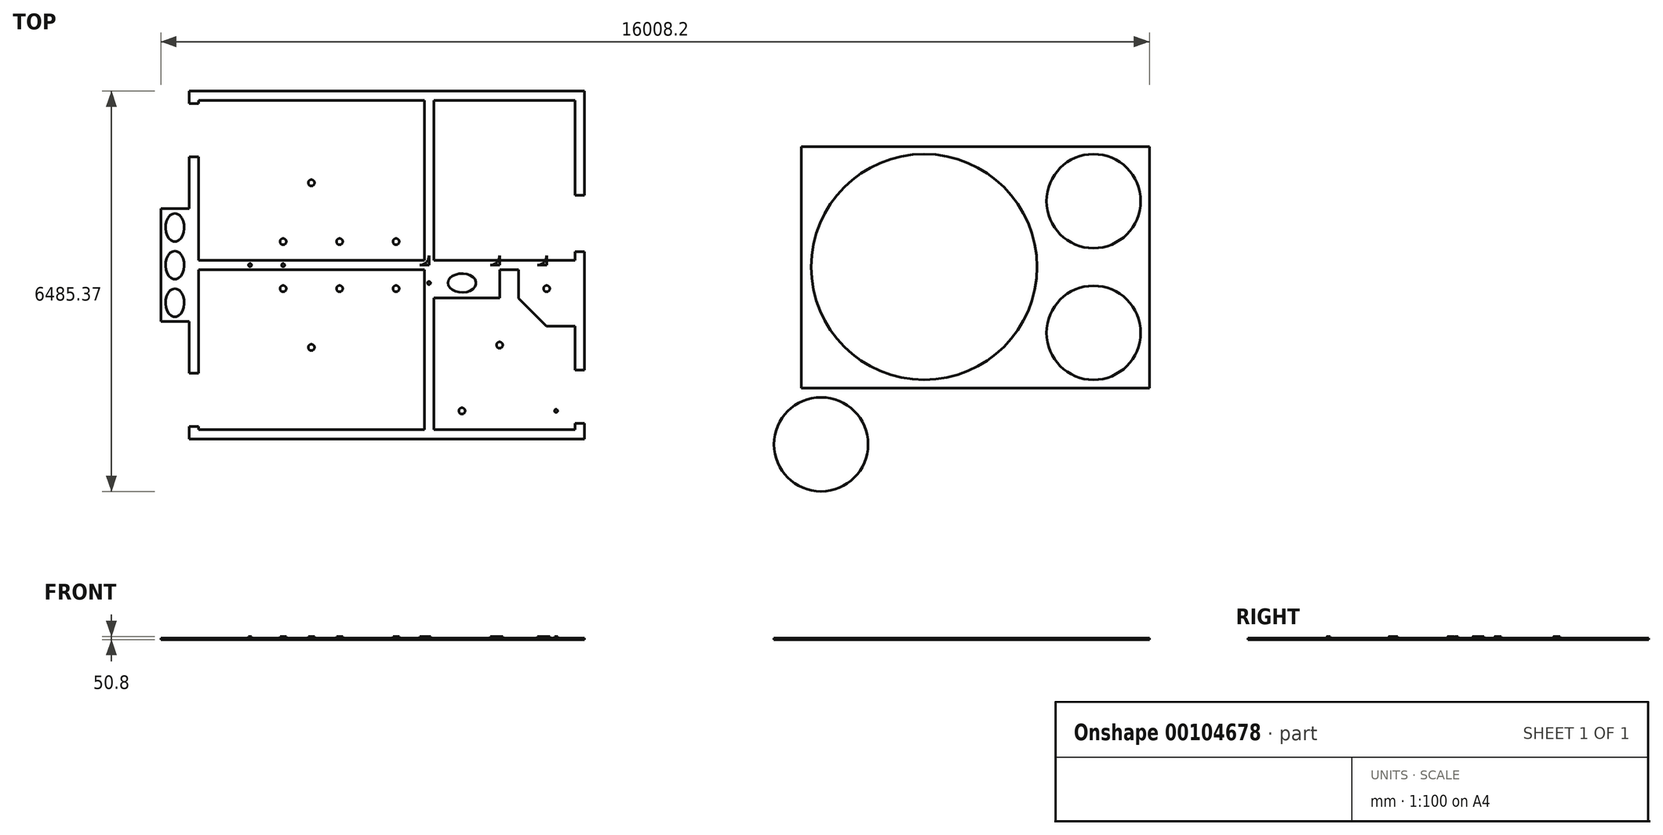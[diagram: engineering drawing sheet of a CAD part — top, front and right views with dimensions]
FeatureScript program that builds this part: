
annotation { "Feature Type Name" : "Feature", "Feature Type Description" : "" }
export const myFeature = defineFeature(function(context is Context, id is Id, definition is map)
    precondition{}
    {
        {
            var Q0;
            Q0=qCreatedBy(makeId("Top.planeOp"),FACE);
            var sketch = newSketch(context, id + "F0", { "sketchPlane" : qUnion([Q0])});
            skLineSegment(sketch, "E0.bottom", {"start": v(0, -6096) * mm, "end": v(7315.2, -6096) * mm, "construction": true});
            skLineSegment(sketch, "E0.left", {"start": v(0, -6096) * mm, "end": v(0, 0) * mm, "construction": true});
            skLineSegment(sketch, "E0.right", {"start": v(7315.2, -6096) * mm, "end": v(7315.2, 0) * mm, "construction": true});
            skLineSegment(sketch, "E1", {"start": v(-8239.1, 0) * mm, "end": v(16647.6, 0) * mm, "construction": true});
            skLineSegment(sketch, "E2", {"start": v(3581.4, 0) * mm, "end": v(3581.4, -228.6) * mm});
            skLineSegment(sketch, "E3", {"start": v(3581.4, -228.6) * mm, "end": v(3733.8, -228.6) * mm});
            skLineSegment(sketch, "E4", {"start": v(3733.8, -228.6) * mm, "end": v(3733.8, 0) * mm});
            skSolve(sketch);
        }
        {
            var Q0;
            Q0=qCreatedBy(makeId("Top.planeOp"),FACE);
            var sketch = newSketch(context, id + "F1", { "sketchPlane" : qUnion([Q0])});
            skLineSegment(sketch, "E5", {"start": v(152.4, -2743.2) * mm, "end": v(3810, -2743.2) * mm});
            skLineSegment(sketch, "E6.MirrorCS", {"start": v(152.4, -2895.6) * mm, "end": v(3810, -2895.6) * mm});
            skLineSegment(sketch, "E7", {"start": v(6400.8, -5638.8) * mm, "end": v(0, -5638.8) * mm});
            skLineSegment(sketch, "E8", {"start": v(0, -4572) * mm, "end": v(0, -1066.8) * mm});
            skLineSegment(sketch, "E9", {"start": v(0, 0) * mm, "end": v(3962.4, 0) * mm});
            skLineSegment(sketch, "E10", {"start": v(3962.4, -152.4) * mm, "end": v(3962.4, -2743.2) * mm});
            skCircle(sketch, "E11", {"center": v(11904.2, -2849.46) * mm, "radius": 1828.8 * mm});
            skCircle(sketch, "E12", {"center": v(14647.4, -3916.26) * mm, "radius": 762 * mm});
            skLineSegment(sketch, "E13", {"start": v(14647.4, -3916.26) * mm, "end": v(14647.4, -1782.66) * mm});
            skCircle(sketch, "E14", {"center": v(14647.4, -1782.66) * mm, "radius": 762 * mm});
            skLineSegment(sketch, "E15", {"start": v(14647.4, -2849.46) * mm, "end": v(11904.2, -2849.46) * mm});
            skLineSegment(sketch, "E16", {"start": v(3962.4, 0) * mm, "end": v(6400.8, 0) * mm});
            skLineSegment(sketch, "E17", {"start": v(6400.8, 0) * mm, "end": v(6400.8, -1687.1) * mm});
            skLineSegment(sketch, "E18", {"start": v(152.4, -2743.2) * mm, "end": v(152.4, -1066.8) * mm});
            skLineSegment(sketch, "E19", {"start": v(3810, -2743.2) * mm, "end": v(3810, -152.4) * mm});
            skLineSegment(sketch, "E20", {"start": v(3810, -152.4) * mm, "end": v(152.4, -152.4) * mm});
            skLineSegment(sketch, "E21", {"start": v(152.4, -1066.8) * mm, "end": v(0, -1066.8) * mm});
            skLineSegment(sketch, "E22.trimOffspring", {"start": v(0, -203.2) * mm, "end": v(0, 0) * mm});
            skLineSegment(sketch, "E23", {"start": v(0, -5638.8) * mm, "end": v(0, -5435.6) * mm});
            skLineSegment(sketch, "E24", {"start": v(3810, -5486.4) * mm, "end": v(3810, -2895.6) * mm});
            skLineSegment(sketch, "E25", {"start": v(2895.6, -2743.2) * mm, "end": v(2895.6, -1219.2) * mm});
            skLineSegment(sketch, "E26", {"start": v(0, -4572) * mm, "end": v(152.4, -4572) * mm});
            skLineSegment(sketch, "E27", {"start": v(152.4, -4572) * mm, "end": v(152.4, -2895.6) * mm});
            skLineSegment(sketch, "E28", {"start": v(1981.2, -2743.2) * mm, "end": v(1981.2, -1219.2) * mm});
            skLineSegment(sketch, "E29", {"start": v(0, -203.2) * mm, "end": v(152.4, -203.2) * mm});
            skLineSegment(sketch, "E30", {"start": v(152.4, -203.2) * mm, "end": v(152.4, -152.4) * mm});
            skLineSegment(sketch, "E31", {"start": v(0, -5435.6) * mm, "end": v(152.4, -5435.6) * mm});
            skLineSegment(sketch, "E32", {"start": v(152.4, -5435.6) * mm, "end": v(152.4, -5486.4) * mm});
            skLineSegment(sketch, "E33.trimOffspring", {"start": v(152.4, -5486.4) * mm, "end": v(3810, -5486.4) * mm});
            skLineSegment(sketch, "E34", {"start": v(1066.8, -2743.2) * mm, "end": v(1066.8, -1219.2) * mm});
            skLineSegment(sketch, "E35", {"start": v(1066.8, -1219.2) * mm, "end": v(1143, -1219.2) * mm});
            skLineSegment(sketch, "E36", {"start": v(1905, -1219.2) * mm, "end": v(2057.4, -1219.2) * mm});
            skLineSegment(sketch, "E37", {"start": v(2819.4, -1219.2) * mm, "end": v(2971.8, -1219.2) * mm});
            skLineSegment(sketch, "E38", {"start": v(1143, -1219.2) * mm, "end": v(1732.48, -1702.06) * mm});
            skLineSegment(sketch, "E39", {"start": v(3810, -1219.2) * mm, "end": v(3733.8, -1219.2) * mm});
            skLineSegment(sketch, "E40", {"start": v(2057.4, -1219.2) * mm, "end": v(2646.88, -1702.06) * mm});
            skLineSegment(sketch, "E41", {"start": v(2971.8, -1219.2) * mm, "end": v(3561.28, -1702.06) * mm});
            skLineSegment(sketch, "E42", {"start": v(76.2, -203.2) * mm, "end": v(589.55, -897.66) * mm});
            skLineSegment(sketch, "E43", {"start": v(6400.8, -2819.4) * mm, "end": v(0, -2819.4) * mm, "construction": true});
            skLineSegment(sketch, "E44.MirrorCS", {"start": v(76.2, -5435.6) * mm, "end": v(589.55, -4741.14) * mm});
            skLineSegment(sketch, "E45.MirrorCS", {"start": v(1066.8, -4419.6) * mm, "end": v(1143, -4419.6) * mm});
            skLineSegment(sketch, "E46.MirrorCS", {"start": v(2819.4, -4419.6) * mm, "end": v(2971.8, -4419.6) * mm});
            skLineSegment(sketch, "E47.MirrorCS", {"start": v(1905, -4419.6) * mm, "end": v(2057.4, -4419.6) * mm});
            skLineSegment(sketch, "E48.MirrorCS", {"start": v(2971.8, -4419.6) * mm, "end": v(3561.28, -3936.74) * mm});
            skLineSegment(sketch, "E49.MirrorCS", {"start": v(1981.2, -2895.6) * mm, "end": v(1981.2, -4419.6) * mm});
            skLineSegment(sketch, "E50.MirrorCS", {"start": v(1066.8, -2895.6) * mm, "end": v(1066.8, -4419.6) * mm});
            skLineSegment(sketch, "E51.MirrorCS", {"start": v(2057.4, -4419.6) * mm, "end": v(2646.88, -3936.74) * mm});
            skLineSegment(sketch, "E52.MirrorCS", {"start": v(2895.6, -2895.6) * mm, "end": v(2895.6, -4419.6) * mm});
            skLineSegment(sketch, "E53.MirrorCS", {"start": v(3810, -4419.6) * mm, "end": v(3733.8, -4419.6) * mm});
            skLineSegment(sketch, "E54.MirrorCS", {"start": v(1143, -4419.6) * mm, "end": v(1732.48, -3936.74) * mm});
            skLineSegment(sketch, "E55", {"start": v(0, -1905) * mm, "end": v(-457.2, -1905) * mm});
            skLineSegment(sketch, "E56", {"start": v(-457.2, -1905) * mm, "end": v(-457.2, -3733.8) * mm});
            skLineSegment(sketch, "E57", {"start": v(-457.2, -3733.8) * mm, "end": v(0, -3733.8) * mm});
            skEllipse(sketch, "E58", {"center": v(-228.6, -2209.8) * mm, "majorRadius": 228.6 * mm, "minorRadius": 152.4 * mm, "majorAxis": v(0, 1)});
            skEllipse(sketch, "E59", {"center": v(-228.6, -2819.4) * mm, "majorRadius": 228.6 * mm, "minorRadius": 152.4 * mm, "majorAxis": v(0, 1)});
            skEllipse(sketch, "E60", {"center": v(-228.6, -3429) * mm, "majorRadius": 228.6 * mm, "minorRadius": 152.4 * mm, "majorAxis": v(0, 1)});
            skLineSegment(sketch, "E61", {"start": v(3962.4, -2895.6) * mm, "end": v(6248.4, -2895.6) * mm});
            skLineSegment(sketch, "E62", {"start": v(6248.4, -2895.6) * mm, "end": v(6248.4, -4521.2) * mm});
            skLineSegment(sketch, "E63.trimOffspring", {"start": v(3962.4, -2895.6) * mm, "end": v(3962.4, -5486.4) * mm});
            skLineSegment(sketch, "E64.trimOffspring", {"start": v(3962.4, -5486.4) * mm, "end": v(6248.4, -5486.4) * mm});
            skLineSegment(sketch, "E65.bottom", {"start": v(15551.04, -4814.37) * mm, "end": v(9912.24, -4814.37) * mm});
            skLineSegment(sketch, "E65.top", {"start": v(15551.04, -902.77) * mm, "end": v(9912.24, -902.77) * mm});
            skLineSegment(sketch, "E65.left", {"start": v(15551.04, -4814.37) * mm, "end": v(15551.04, -902.77) * mm});
            skLineSegment(sketch, "E65.right", {"start": v(9912.24, -4814.37) * mm, "end": v(9912.24, -902.77) * mm});
            skEllipse(sketch, "E66", {"center": v(4419.6, -3109.6) * mm, "majorRadius": 228.6 * mm, "minorRadius": 152.4 * mm, "majorAxis": v(-1, 0)});
            skLineSegment(sketch, "E67", {"start": v(3962.4, -3352.8) * mm, "end": v(5029.2, -3352.8) * mm});
            skLineSegment(sketch, "E68", {"start": v(6248.4, -3810) * mm, "end": v(5784.85, -3810) * mm});
            skCircle(sketch, "E69", {"center": v(10234.54, -5723.37) * mm, "radius": 762 * mm});
            skLineSegment(sketch, "E70", {"start": v(5334, -3359.15) * mm, "end": v(5784.85, -3810) * mm});
            skLineSegment(sketch, "E71.trimOffspring", {"start": v(5334, -3359.15) * mm, "end": v(5334, -2895.6) * mm});
            skLineSegment(sketch, "E72", {"start": v(3962.4, -152.4) * mm, "end": v(6248.4, -152.4) * mm});
            skLineSegment(sketch, "E73", {"start": v(6248.4, -152.4) * mm, "end": v(6248.4, -1687.1) * mm});
            skLineSegment(sketch, "E74", {"start": v(6248.4, -2743.2) * mm, "end": v(3962.4, -2743.2) * mm});
            skLineSegment(sketch, "E75", {"start": v(6248.4, -2601.5) * mm, "end": v(6400.8, -2601.5) * mm});
            skLineSegment(sketch, "E76", {"start": v(6248.4, -1687.1) * mm, "end": v(6400.8, -1687.1) * mm});
            skLineSegment(sketch, "E77.trimOffspring", {"start": v(6248.4, -2601.5) * mm, "end": v(6248.4, -2743.2) * mm});
            skLineSegment(sketch, "E78.trimOffspring", {"start": v(6400.8, -2601.5) * mm, "end": v(6400.8, -4521.2) * mm});
            skLineSegment(sketch, "E79", {"start": v(5029.2, -3352.8) * mm, "end": v(5029.2, -2895.6) * mm});
            skCircle(sketch, "E80", {"center": v(4419.6, -5181.6) * mm, "radius": 50.8 * mm});
            skLineSegment(sketch, "E81", {"start": v(6248.4, -5384.8) * mm, "end": v(6400.8, -5384.8) * mm});
            skLineSegment(sketch, "E82", {"start": v(6248.4, -4521.2) * mm, "end": v(6400.8, -4521.2) * mm});
            skLineSegment(sketch, "E83.trimOffspring", {"start": v(6400.8, -5384.8) * mm, "end": v(6400.8, -5638.8) * mm});
            skLineSegment(sketch, "E84.trimOffspring", {"start": v(6248.4, -5384.8) * mm, "end": v(6248.4, -5486.4) * mm});
            skLineSegment(sketch, "E85", {"start": v(6324.6, -5384.8) * mm, "end": v(5921.52, -4621.04) * mm});
            skLineSegment(sketch, "E86", {"start": v(6324.6, -2601.5) * mm, "end": v(5876.55, -1804.4) * mm});
            skPoint(sketch, "E87", {"position": v(5105.4, -1447.8) * mm});
            skLineSegment(sketch, "E88", {"start": v(5105.4, -1447.8) * mm, "end": v(4404.46, -2148.74) * mm});
            skLineSegment(sketch, "E89", {"start": v(5105.4, -1447.8) * mm, "end": v(5105.4, -2236.51) * mm, "construction": true});
            skSolve(sketch);
        }
        {
            var Q0;
            Q0=qCreatedBy(makeId("Top.planeOp"),FACE);
            var sketch = newSketch(context, id + "F2", { "sketchPlane" : qUnion([Q0])});
            skLineSegment(sketch, "E90", {"start": v(5791.2, -2667) * mm, "end": v(5791.2, -3251.2) * mm});
            skCircle(sketch, "E91", {"center": v(1524, -2438.4) * mm, "radius": 50.8 * mm});
            skCircle(sketch, "E92", {"center": v(1524, -3200.4) * mm, "radius": 50.8 * mm});
            skCircle(sketch, "E93", {"center": v(2438.4, -3200.4) * mm, "radius": 50.8 * mm});
            skCircle(sketch, "E94", {"center": v(2438.4, -2438.4) * mm, "radius": 50.8 * mm});
            skCircle(sketch, "E95", {"center": v(3352.8, -2438.4) * mm, "radius": 50.8 * mm});
            skCircle(sketch, "E96", {"center": v(3352.8, -3200.4) * mm, "radius": 50.8 * mm});
            skCircle(sketch, "E97", {"center": v(5791.2, -3200.4) * mm, "radius": 50.8 * mm});
            skCircle(sketch, "E98", {"center": v(3886.2, -3109.6) * mm, "radius": 25.4 * mm});
            skCircle(sketch, "E99", {"center": v(988.97, -2819.4) * mm, "radius": 25.4 * mm});
            skCircle(sketch, "E100", {"center": v(1981.2, -4152.9) * mm, "radius": 50.8 * mm});
            skCircle(sketch, "E101", {"center": v(1981.2, -1485.9) * mm, "radius": 50.8 * mm});
            skCircle(sketch, "E102", {"center": v(5029.2, -4114.8) * mm, "radius": 50.8 * mm});
            skLineSegment(sketch, "E103", {"start": v(1981.2, -1485.9) * mm, "end": v(1981.2, -2794.35) * mm});
            skLineSegment(sketch, "E104", {"start": v(1981.2, -4152.9) * mm, "end": v(1981.2, -2844.46) * mm});
            skLineSegment(sketch, "E105", {"start": v(5029.2, -2667) * mm, "end": v(5029.2, -4165.6) * mm});
            skLineSegment(sketch, "E106", {"start": v(0, -2819.4) * mm, "end": v(1834.75, -2819.4) * mm});
            skLineSegment(sketch, "E107", {"start": v(1524, -2489.2) * mm, "end": v(1524, -2813.12) * mm});
            skLineSegment(sketch, "E108", {"start": v(2438.4, -2489.2) * mm, "end": v(2438.4, -2667) * mm});
            skLineSegment(sketch, "E109", {"start": v(2438.4, -2971.8) * mm, "end": v(2438.4, -3149.6) * mm});
            skLineSegment(sketch, "E110", {"start": v(3352.8, -2489.2) * mm, "end": v(3352.8, -2667) * mm});
            skLineSegment(sketch, "E111", {"start": v(3352.8, -2971.8) * mm, "end": v(3352.8, -3149.6) * mm});
            skLineSegment(sketch, "E112", {"start": v(1979.13, -2819.4) * mm, "end": v(2286, -2819.4) * mm});
            skArc(sketch, "E113.filletArc", {"start": v(2286, -2819.4) * mm, "mid": v(2393.76, -2774.76) * mm, "end": v(2438.4, -2667) * mm});
            skArc(sketch, "E114.filletArc", {"start": v(2438.4, -2971.8) * mm, "mid": v(2393.76, -2864.04) * mm, "end": v(2286, -2819.4) * mm});
            skLineSegment(sketch, "E115", {"start": v(2286, -2819.4) * mm, "end": v(3200.4, -2819.4) * mm});
            skArc(sketch, "E116.filletArc", {"start": v(3200.4, -2819.4) * mm, "mid": v(3308.16, -2774.76) * mm, "end": v(3352.8, -2667) * mm});
            skArc(sketch, "E117.filletArc", {"start": v(3352.8, -2971.8) * mm, "mid": v(3308.16, -2864.04) * mm, "end": v(3200.4, -2819.4) * mm});
            skLineSegment(sketch, "E118", {"start": v(3200.4, -2819.4) * mm, "end": v(3733.8, -2819.4) * mm});
            skLineSegment(sketch, "E119", {"start": v(3733.8, -2819.4) * mm, "end": v(4876.8, -2819.4) * mm});
            skLineSegment(sketch, "E120", {"start": v(4876.8, -2819.4) * mm, "end": v(5638.8, -2819.4) * mm});
            skArc(sketch, "E121.filletArc", {"start": v(4876.8, -2819.4) * mm, "mid": v(4984.56, -2774.76) * mm, "end": v(5029.2, -2667) * mm});
            skArc(sketch, "E122.filletArc", {"start": v(5638.8, -2819.4) * mm, "mid": v(5746.56, -2774.76) * mm, "end": v(5791.2, -2667) * mm});
            skCircle(sketch, "E123", {"center": v(1524, -2819.4) * mm, "radius": 25.4 * mm});
            skCircle(sketch, "E124", {"center": v(5943.6, -5181.6) * mm, "radius": 25.4 * mm});
            skLineSegment(sketch, "E125", {"start": v(5943.6, -2667) * mm, "end": v(5943.6, -5181.6) * mm});
            skLineSegment(sketch, "E126", {"start": v(5791.2, -2819.4) * mm, "end": v(5638.8, -2819.4) * mm});
            skArc(sketch, "E127.filletArc", {"start": v(5791.2, -2819.4) * mm, "mid": v(5898.96, -2774.76) * mm, "end": v(5943.6, -2667) * mm});
            skLineSegment(sketch, "E128", {"start": v(4419.6, -3109.6) * mm, "end": v(3886.2, -3109.6) * mm});
            skLineSegment(sketch, "E129", {"start": v(3886.2, -2667) * mm, "end": v(3886.2, -3135) * mm});
            skArc(sketch, "E130.filletArc", {"start": v(3733.8, -2819.4) * mm, "mid": v(3841.56, -2774.76) * mm, "end": v(3886.2, -2667) * mm});
            skSolve(sketch);
        }
        {
            var Q0;
            Q0=qSketchRegion(id+"F1",true);
            extrude(context, id + "F3", {"entities" : qUnion([Q0]), "depth" : 25.4 * mm, "offsetDistance" : 25.4 * mm});
        }
        {
            var Q0;
            Q0=qSketchRegion(id+"F2",true);
            extrude(context, id + "F4", {"entities" : qUnion([Q0]), "operationType" : NewBodyOperationType.ADD, "depth" : 50.8 * mm, "offsetDistance" : 25.4 * mm});
        }
    });
